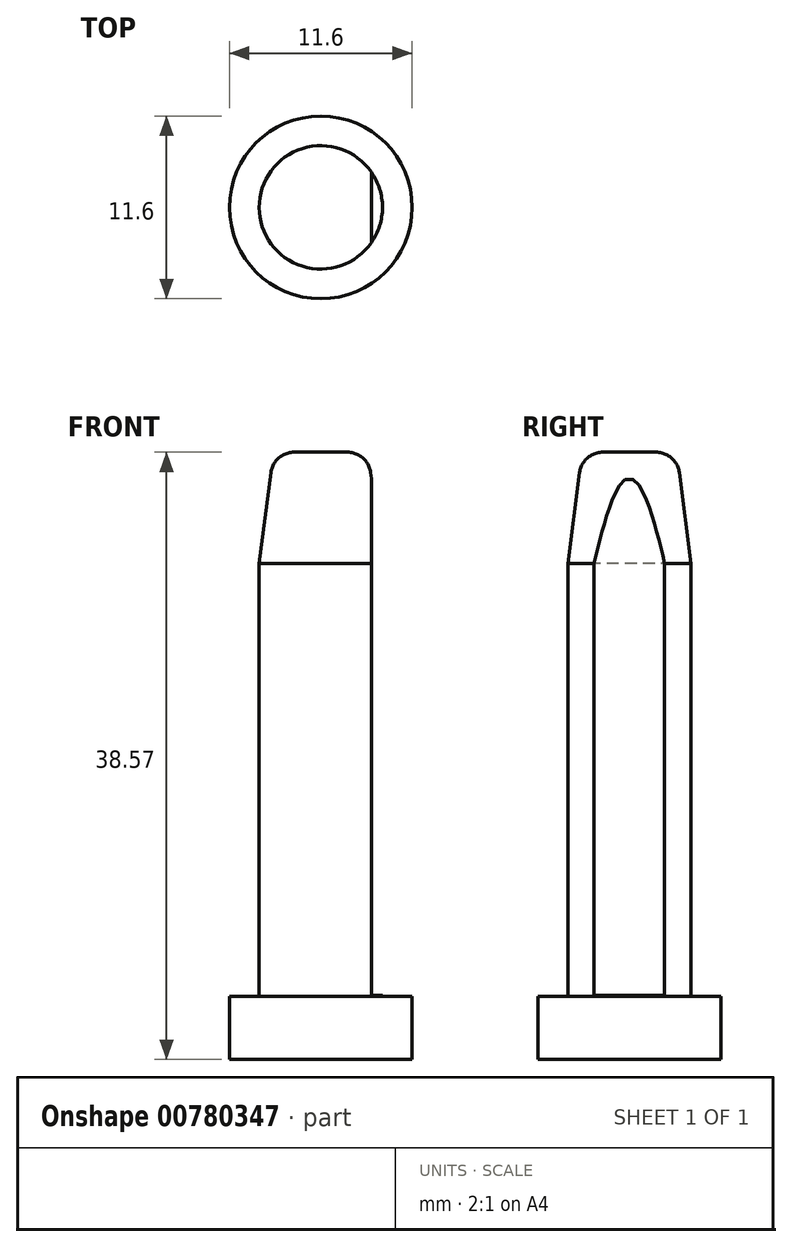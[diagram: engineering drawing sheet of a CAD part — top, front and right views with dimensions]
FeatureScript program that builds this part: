
annotation { "Feature Type Name" : "Feature", "Feature Type Description" : "" }
export const myFeature = defineFeature(function(context is Context, id is Id, definition is map)
    precondition{}
    {
        {
            var Q0;
            Q0=qCreatedBy(makeId("Front.planeOp"),FACE);
            var sketch = newSketch(context, id + "F0", { "sketchPlane" : qUnion([Q0])});
            skLineSegment(sketch, "E0", {"start": v(0, 0) * mm, "end": v(-5.8, 0) * mm});
            skLineSegment(sketch, "E1", {"start": v(-5.8, 0) * mm, "end": v(-5.8, 4) * mm});
            skLineSegment(sketch, "E2", {"start": v(-5.8, 4) * mm, "end": v(-3.92, 4) * mm});
            skLineSegment(sketch, "E3", {"start": v(-3.92, 4) * mm, "end": v(-3.92, 31.5) * mm});
            skLineSegment(sketch, "E4", {"start": v(-3, 38.57) * mm, "end": v(0, 38.57) * mm});
            skLineSegment(sketch, "E5", {"start": v(-3.92, 31.5) * mm, "end": v(-3, 38.57) * mm});
            skLineSegment(sketch, "E6", {"start": v(0, 40.24) * mm, "end": v(0, -3.84) * mm, "construction": true});
            skLineSegment(sketch, "E7", {"start": v(0, 38.57) * mm, "end": v(0, 0) * mm});
            skSolve(sketch);
        }
        {
            var Q0;
            Q0=makeQuery(id+"F0.imprint","IMPRINT",FACE,{"disambiguationData":[TD([[makeQuery(id+"F0.imprint","IMPRINT",EDGE,{"derivedFrom":sQuery(id+"F0.wireOp",EDGE,"E0")}),-1.0]])]});
            var Q1;
            Q1=sQuery(id+"F0.wireOp",EDGE,"E7");
            revolve(context, id + "F1", {"surfaceOperationType" : NewSurfaceOperationType.NEW, "entities" : qUnion([Q0]), "axis" : qUnion([Q1]), "revolveType" : RevolveType.FULL});
        }
        {
            var Q0;
            Q0=qCreatedBy(makeId("Right.planeOp"),FACE);
            cPlane(context, id + "F2", {"entities" : qUnion([Q0]), "cplaneType" : CPlaneType.OFFSET, "offset" : 3.21 * mm, "width" : 150 * mm, "height" : 150 * mm});
        }
        {
            var Q0;
            Q0=qCreatedBy(id+"F2.planeOp",FACE);
            var sketch = newSketch(context, id + "F3", { "sketchPlane" : qUnion([Q0])});
            skLineSegment(sketch, "E8", {"start": v(-4.2, 4.07) * mm, "end": v(4.51, 4.07) * mm});
            skLineSegment(sketch, "E9", {"start": v(4.51, 4.07) * mm, "end": v(4.87, 39.2) * mm});
            skLineSegment(sketch, "E10", {"start": v(-4.2, 4.07) * mm, "end": v(-4.2, 39.2) * mm});
            skLineSegment(sketch, "E11", {"start": v(-4.2, 39.2) * mm, "end": v(4.87, 39.2) * mm});
            skSolve(sketch);
        }
        {
            var Q0;
            Q0 = qSketchRegion(id + "F3", true);
            extrude(context, id + "F4", {"entities" : qUnion([Q0]), "operationType" : NewBodyOperationType.REMOVE, "depth" : 9.6 * mm, "offsetDistance" : 25 * mm});
        }
        {
            var Q0;
            Q0=makeQuery(id+"F1.opRevolve","SWEPT_EDGE",EDGE,{"disambiguationData":[OSD([sQuery(id+"F0.wireOp",EDGE,"E4"),sQuery(id+"F0.wireOp",EDGE,"E5")])]});
            fillet(context, id + "F5", {"entities" : qUnion([Q0]), "radius" : 1.48 * mm, "tangentPropagation" : true, "allowEdgeOverflow" : false});
        }
    });
